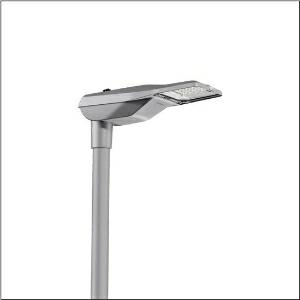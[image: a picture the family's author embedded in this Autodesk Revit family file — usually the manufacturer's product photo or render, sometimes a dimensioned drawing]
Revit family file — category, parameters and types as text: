
# Revit family: streetlight_sl_21_micro___stw1_0a_5xe1e43s08db_ea06
name_source: partatom
category: Lighting Fixtures
units: mm (PartAtom-declared; Revit-internal decimal feet)

## family parameters
Cut with Voids When Loaded = No
Host = Face
Light Source = No
Part Type = Normal
Room Calculation Point = No
Round Connector Dimension = Use Diameter
Shared = No

## types (1)
- --- (1 x LED, 5320 lm, 39.1 W, 4000K)
    Apparent Load = 39 VA
    CIE Flux Codes = 38 75 98 100 100
    Color Rendering = 70
    Color Temperature = 4000K
    Default Elevation = 1800 mm
    Description = Streetlight SL 21 micro, mast luminaire, primary light control with lens, of PMMA, primary optical cover: cover, of toughened safety glass, transparent, light distribution: STW1.0a, light emission: direct distribution, primary light characteristic: asymmetric, installation type: side-entry, post-top, LED, High Power LED, rated luminous flux: 5.320lm, luminous efficacy: 136lm/W, light colour: 740, colour temperature: 4000K, control gear: D4i, control: flexible luminous flux parameterisation, time-dependent luminous flux control, constant luminous flux control, overheat protection, pre-setting: logarithmic dimming characteristic, mains connection: 220..240V, AC, 50/60Hz, start of lifetime: 39W, end of service life: 41W, reduction: 18W, luminaire housing, of diecast aluminium, powder-coated, Siteco® metallic grey (DB 702S), corrosivity category C5 mid according to DIN EN ISO 12944, please order mast flange separately, inclination adjustable: 0°, 5°, 10°, 15°, sealing non-destructively replaceable, multi-level sealing system, length: 528mm, width: 235mm, height: 110mm, mast flange for spigot size: 42mm (side-entry): 5XC10008XM4, 60/48mm (side-entry/post-top): 5XC10108XM2, 76/60mm (side-entry/post-top): 5XC10108XM1, Smart Interface above, protection rating (complete): IP66, insulation class (complete): insulation class II (safety insulation), certification: CE, ENEC, ENEC+, VDE, impact resistance: IK10, permissible operating ambient temperature for outdoor applications: -40..+50°C, standard-compliant lighting for roads and squares, packaging unit: 1 piece

Light Distribution: STW1.0a
    Height = 110 mm
    Lamp = 1 x LED
    Lamp Light Flux = 5320 lm
    Lamp Power = 39.1 W
    Lamp count = 1
    Length = 528 mm
    Luminous efficacy = 136 lm/W
    Manufacturer = Siteco
    ModVariant = No
    Model = 5XE1E43S08DB
    Number of Poles = 1
    OnlyDefault = Yes
    Power Factor = 1
    Product Name = Streetlight SL 21 micro | STW1.0a
    Product group = mast luminaire | pylon top
    ProductGroupID = 6100
    Protection Class = Protection class II
    Protection Degree = IP 66
    RLX_Detail_Level = 1
    RLX_Emergency_Light_Flux = 0 lm
    RLX_Emergency_Type = 0
    RLX_Emergency_Type_DB = No
    RlxData = <blob elided: 98213 chars, md5=3c80be4a>
    Socket = socket
    Standby Power = 0 W
    System Light Flux = 5320 lm
    System Power = 39 W
    Type Comments = factory setting: luminous flux: 100 % | dim-lin: 254 | 765 mA
    Type Image = l_1277292.jpg
    URL = http://relux.com
    VarID = @adj_155348
    Voltage = 0 V
    Weight = 0.00 kg
    Width = 235 mm

## geometry (parser evidence)
native form markers: Blend x4, Sweep x10
no freeform markers — native parametric forms only
